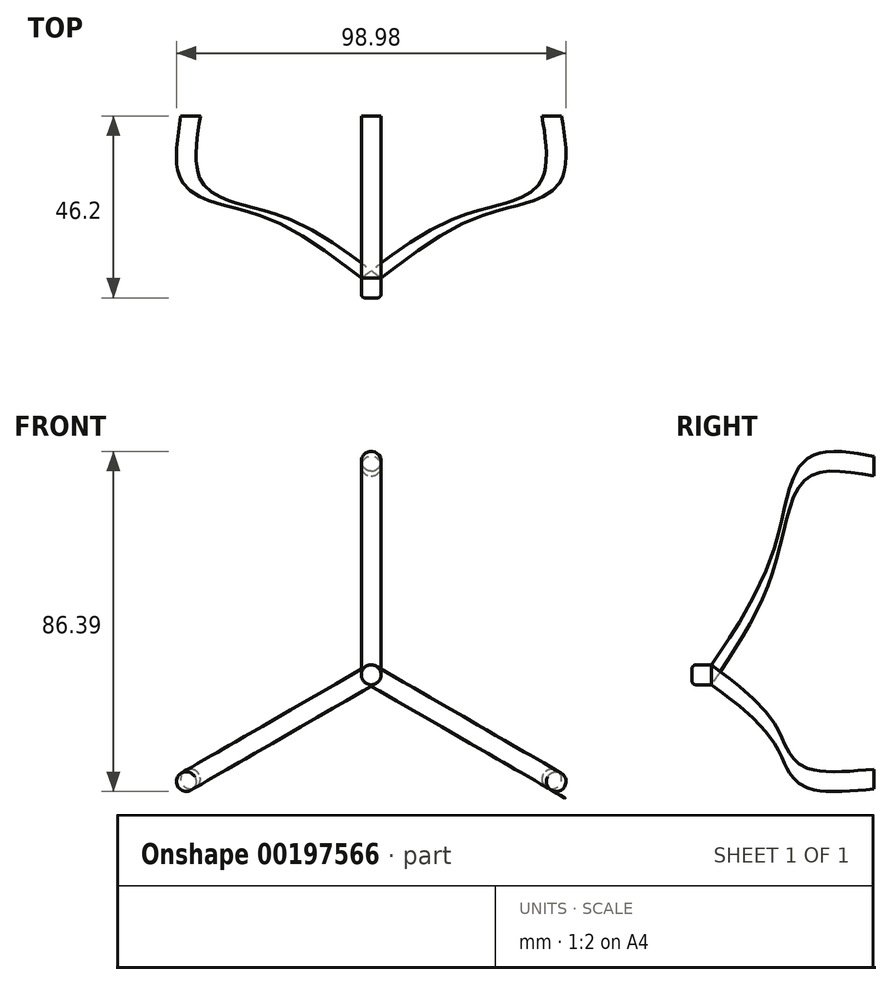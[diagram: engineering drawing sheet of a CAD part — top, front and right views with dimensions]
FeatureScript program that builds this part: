
annotation { "Feature Type Name" : "Feature", "Feature Type Description" : "" }
export const myFeature = defineFeature(function(context is Context, id is Id, definition is map)
    precondition{}
    {
        {
            var Q0;
            Q0=qCreatedBy(makeId("Front.planeOp"),FACE);
            var sketch = newSketch(context, id + "F0", { "sketchPlane" : qUnion([Q0])});
            skPoint(sketch, "E0.center", {"position": v(0, 0) * mm});
            skCircle(sketch, "E1", {"center": v(0, 53) * mm, "radius": 2.5 * mm});
            skCircle(sketch, "E2.1.0", {"center": v(-45.9, -26.5) * mm, "radius": 2.5 * mm});
            skCircle(sketch, "E2.2.0", {"center": v(45.9, -26.5) * mm, "radius": 2.5 * mm});
            skSolve(sketch);
        }
        {
            var Q0;
            Q0=qCreatedBy(makeId("Right.planeOp"),FACE);
            var sketch = newSketch(context, id + "F1", { "sketchPlane" : qUnion([Q0])});
            skFitSpline(sketch, "E3", {"points": [v(0, 52.98) * mm, v(-17.25, 52.18) * mm, v(-25.44, 29.18) * mm, v(-41.2, 0) * mm], "startDerivative": vector(-71.59, 12.96) * mm, "endDerivative": vector(-48.14, -71.87) * mm});
            skSolve(sketch);
        }
        {
            var Q0;
            Q0=qCreatedBy(makeId("Top.planeOp"),FACE);
            var sketch = newSketch(context, id + "F2", { "sketchPlane" : qUnion([Q0])});
            skLineSegment(sketch, "E4", {"start": v(0, 0) * mm, "end": v(0, -34.03) * mm});
            skSolve(sketch);
        }
        {
            var Q0;
            Q0=makeQuery(id+"F0.imprint","IMPRINT",FACE,{"disambiguationData":[TD([[makeQuery(id+"F0.imprint","IMPRINT",EDGE,{"derivedFrom":sQuery(id+"F0.wireOp",EDGE,"E1")}),1.0]])]});
            var Q1;
            Q1=sQuery(id+"F1.wireOp",EDGE,"E3");
            sweep(context, id + "F3", {"profiles" : qUnion([Q0]), "path" : qUnion([Q1]), "keepProfileOrientation" : true});
        }
        {
            var Q0;
            Q0=makeQuery(id+"F3.opSweep","SWEPT_BODY",BODY,{"disambiguationData":[OSD([sQuery(id+"F0.wireOp",EDGE,"E1"),sQuery(id+"F1.wireOp",EDGE,"E3")])]});
            var Q1;
            Q1=sQuery(id+"F2.wireOp",EDGE,"E4");
            circularPattern(context, id + "F4", {"entities" : qUnion([Q0]), "axis" : qUnion([Q1]), "angle" : 360 * degree, "instanceCount" : 3, "equalSpace" : true});
        }
        {
            var Q0;
            Q0=makeQuery(id+"F4.opPattern","COPY",FACE,{"derivedFrom":makeQuery(id+"F3.opSweep","CAP_FACE",FACE,{"disambiguationData":[OSD([sQuery(id+"F0.wireOp",EDGE,"E1"),sQuery(id+"F1.wireOp",VERTEX,"E3.end")])],"isStart":false}),"instanceName":"1"});
            var sketch = newSketch(context, id + "F5", { "sketchPlane" : qUnion([Q0])});
            skCircle(sketch, "E5", {"center": v(0, 0) * mm, "radius": 2.52 * mm});
            skSolve(sketch);
        }
        {
            var Q0;
            Q0 = qSketchRegion(id + "F5", true);
            extrude(context, id + "F6", {"entities" : qUnion([Q0]), "depth" : 5 * mm});
        }
        {
            var Q0;
            Q0=makeQuery(id+"F6.opExtrude","CAP_FACE",FACE,{"disambiguationData":[OSD([sQuery(id+"F5.wireOp",EDGE,"E5")])],"isStart":false});
            fillet(context, id + "F7", {"entities" : qUnion([Q0]), "radius" : 1 * mm, "tangentPropagation" : true, "allowEdgeOverflow" : false});
        }
    });
